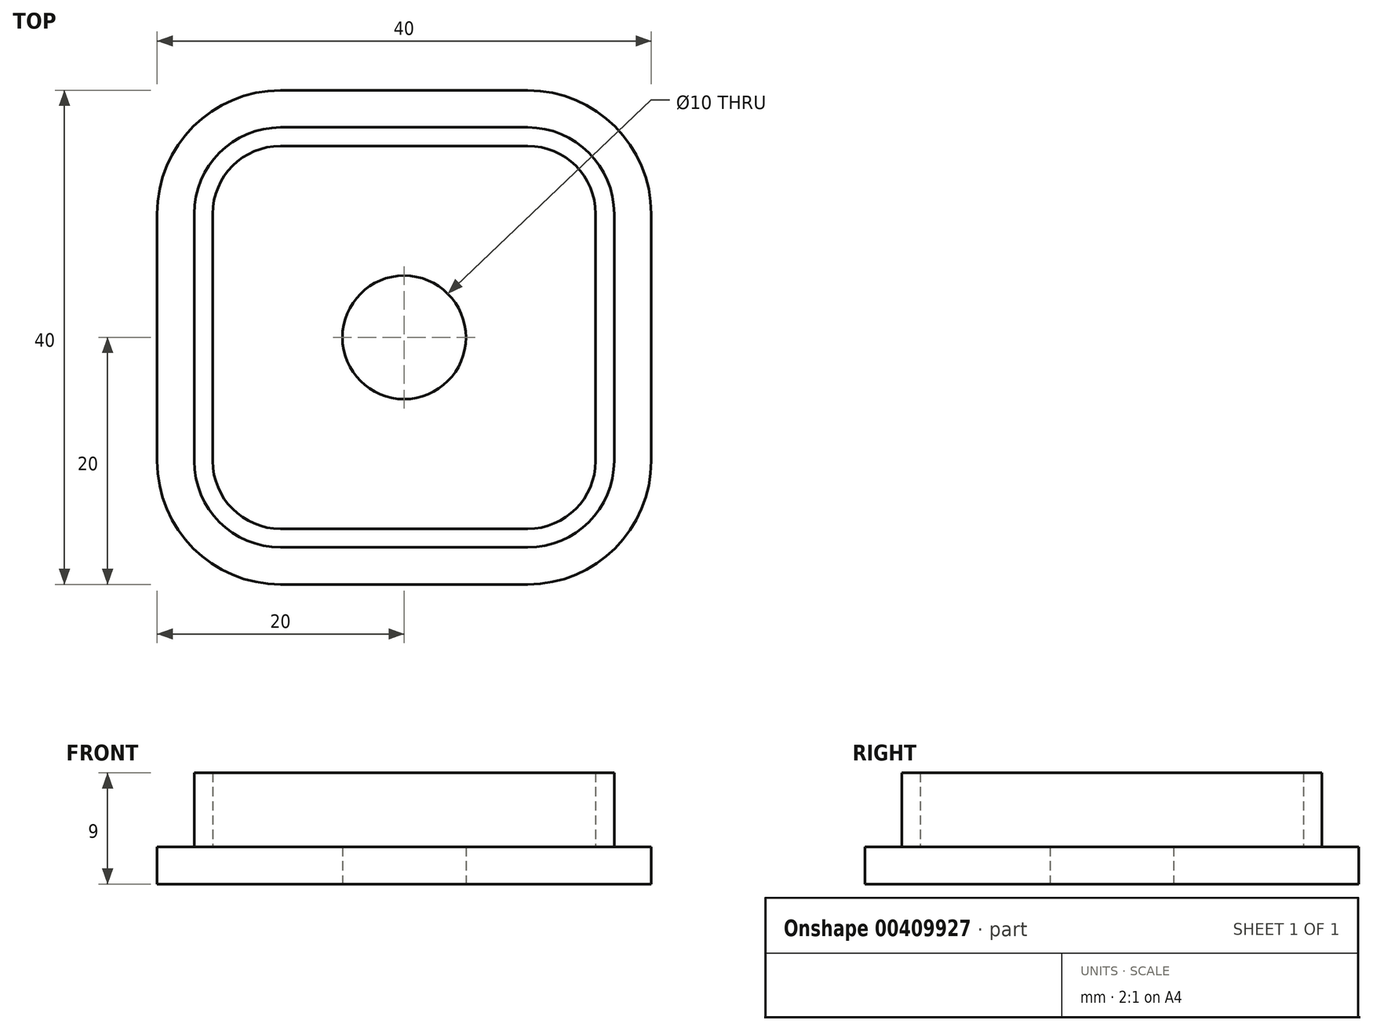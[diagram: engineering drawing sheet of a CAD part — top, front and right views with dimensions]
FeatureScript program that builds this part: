
annotation { "Feature Type Name" : "Feature", "Feature Type Description" : "" }
export const myFeature = defineFeature(function(context is Context, id is Id, definition is map)
    precondition{}
    {
        {
            var Q0;
            Q0=qCreatedBy(makeId("Top.planeOp"),FACE);
            var sketch = newSketch(context, id + "F0", { "sketchPlane" : qUnion([Q0])});
            skLineSegment(sketch, "E0.bottom", {"start": v(10, 20) * mm, "end": v(-10, 20) * mm});
            skLineSegment(sketch, "E0.top", {"start": v(10, -20) * mm, "end": v(-10, -20) * mm});
            skLineSegment(sketch, "E0.left", {"start": v(20, 10) * mm, "end": v(20, -10) * mm});
            skLineSegment(sketch, "E0.right", {"start": v(-20, 10) * mm, "end": v(-20, -10) * mm});
            skPoint(sketch, "E0.middle", {"position": v(0, 0) * mm});
            skCircle(sketch, "E1", {"center": v(0, 0) * mm, "radius": 5 * mm});
            skPoint(sketch, "E2.visualSharp", {"position": v(-20, 20) * mm});
            skArc(sketch, "E2.filletArc", {"start": v(-10, 20) * mm, "mid": v(-17.07, 17.07) * mm, "end": v(-20, 10) * mm});
            skPoint(sketch, "E3.visualSharp", {"position": v(20, 20) * mm});
            skArc(sketch, "E3.filletArc", {"start": v(20, 10) * mm, "mid": v(17.07, 17.07) * mm, "end": v(10, 20) * mm});
            skPoint(sketch, "E4.visualSharp", {"position": v(20, -20) * mm});
            skArc(sketch, "E4.filletArc", {"start": v(10, -20) * mm, "mid": v(17.07, -17.07) * mm, "end": v(20, -10) * mm});
            skPoint(sketch, "E5.visualSharp", {"position": v(-20, -20) * mm});
            skArc(sketch, "E5.filletArc", {"start": v(-20, -10) * mm, "mid": v(-17.07, -17.07) * mm, "end": v(-10, -20) * mm});
            skSolve(sketch);
        }
        {
            var Q0;
            Q0=makeQuery(id+"F0.imprint","IMPRINT",FACE,{"disambiguationData":[TD([[makeQuery(id+"F0.imprint","IMPRINT",EDGE,{"derivedFrom":sQuery(id+"F0.wireOp",EDGE,"E0.bottom")}),1.0]])]});
            extrude(context, id + "F1", {"entities" : qUnion([Q0]), "depth" : 3 * mm});
        }
        {
            var Q0;
            Q0=makeQuery(id+"F1.opExtrude","CAP_FACE",FACE,{"disambiguationData":[OSD([sQuery(id+"F0.wireOp",EDGE,"E0.bottom"),sQuery(id+"F0.wireOp",EDGE,"E0.top"),sQuery(id+"F0.wireOp",EDGE,"E0.left"),sQuery(id+"F0.wireOp",EDGE,"E0.right"),sQuery(id+"F0.wireOp",EDGE,"E1"),sQuery(id+"F0.wireOp",EDGE,"E2.filletArc"),sQuery(id+"F0.wireOp",EDGE,"E3.filletArc"),sQuery(id+"F0.wireOp",EDGE,"E4.filletArc"),sQuery(id+"F0.wireOp",EDGE,"E5.filletArc")])],"isStart":false});
            var sketch = newSketch(context, id + "F2", { "sketchPlane" : qUnion([Q0])});
            skLineSegment(sketch, "E6.bottom", {"start": v(10, 17) * mm, "end": v(-10, 17) * mm});
            skLineSegment(sketch, "E6.top", {"start": v(10, -17) * mm, "end": v(-10, -17) * mm});
            skLineSegment(sketch, "E6.left", {"start": v(17, 10) * mm, "end": v(17, -10) * mm});
            skLineSegment(sketch, "E6.right", {"start": v(-17, 10) * mm, "end": v(-17, -10) * mm});
            skPoint(sketch, "E6.middle", {"position": v(0, 0) * mm});
            skPoint(sketch, "E7.visualSharp", {"position": v(-17, 17) * mm});
            skArc(sketch, "E7.filletArc", {"start": v(-10, 17) * mm, "mid": v(-14.95, 14.95) * mm, "end": v(-17, 10) * mm});
            skPoint(sketch, "E8.visualSharp", {"position": v(17, 17) * mm});
            skArc(sketch, "E8.filletArc", {"start": v(17, 10) * mm, "mid": v(14.95, 14.95) * mm, "end": v(10, 17) * mm});
            skPoint(sketch, "E9.visualSharp", {"position": v(17, -17) * mm});
            skArc(sketch, "E9.filletArc", {"start": v(10, -17) * mm, "mid": v(14.95, -14.95) * mm, "end": v(17, -10) * mm});
            skPoint(sketch, "E10.visualSharp", {"position": v(-17, -17) * mm});
            skArc(sketch, "E10.filletArc", {"start": v(-17, -10) * mm, "mid": v(-14.95, -14.95) * mm, "end": v(-10, -17) * mm});
            skLineSegment(sketch, "E11.bottom", {"start": v(10, 15.5) * mm, "end": v(-10, 15.5) * mm});
            skLineSegment(sketch, "E11.top", {"start": v(10, -15.5) * mm, "end": v(-10, -15.5) * mm});
            skLineSegment(sketch, "E11.left", {"start": v(15.5, 10) * mm, "end": v(15.5, -10) * mm});
            skLineSegment(sketch, "E11.right", {"start": v(-15.5, 10) * mm, "end": v(-15.5, -10) * mm});
            skPoint(sketch, "E12.visualSharp", {"position": v(-15.5, 15.5) * mm});
            skArc(sketch, "E12.filletArc", {"start": v(-10, 15.5) * mm, "mid": v(-13.89, 13.89) * mm, "end": v(-15.5, 10) * mm});
            skPoint(sketch, "E13.visualSharp", {"position": v(15.5, 15.5) * mm});
            skArc(sketch, "E13.filletArc", {"start": v(15.5, 10) * mm, "mid": v(13.89, 13.89) * mm, "end": v(10, 15.5) * mm});
            skPoint(sketch, "E14.visualSharp", {"position": v(15.5, -15.5) * mm});
            skArc(sketch, "E14.filletArc", {"start": v(10, -15.5) * mm, "mid": v(13.89, -13.89) * mm, "end": v(15.5, -10) * mm});
            skPoint(sketch, "E15.visualSharp", {"position": v(-15.5, -15.5) * mm});
            skArc(sketch, "E15.filletArc", {"start": v(-15.5, -10) * mm, "mid": v(-13.89, -13.89) * mm, "end": v(-10, -15.5) * mm});
            skSolve(sketch);
        }
        {
            var Q0;
            Q0=makeQuery(id+"F2.imprint","IMPRINT",FACE,{"disambiguationData":[TD([[makeQuery(id+"F2.imprint","IMPRINT",EDGE,{"derivedFrom":sQuery(id+"F2.wireOp",EDGE,"E6.bottom")}),1.0]])]});
            extrude(context, id + "F3", {"entities" : qUnion([Q0]), "operationType" : NewBodyOperationType.ADD, "depth" : 6 * mm});
        }
    });
